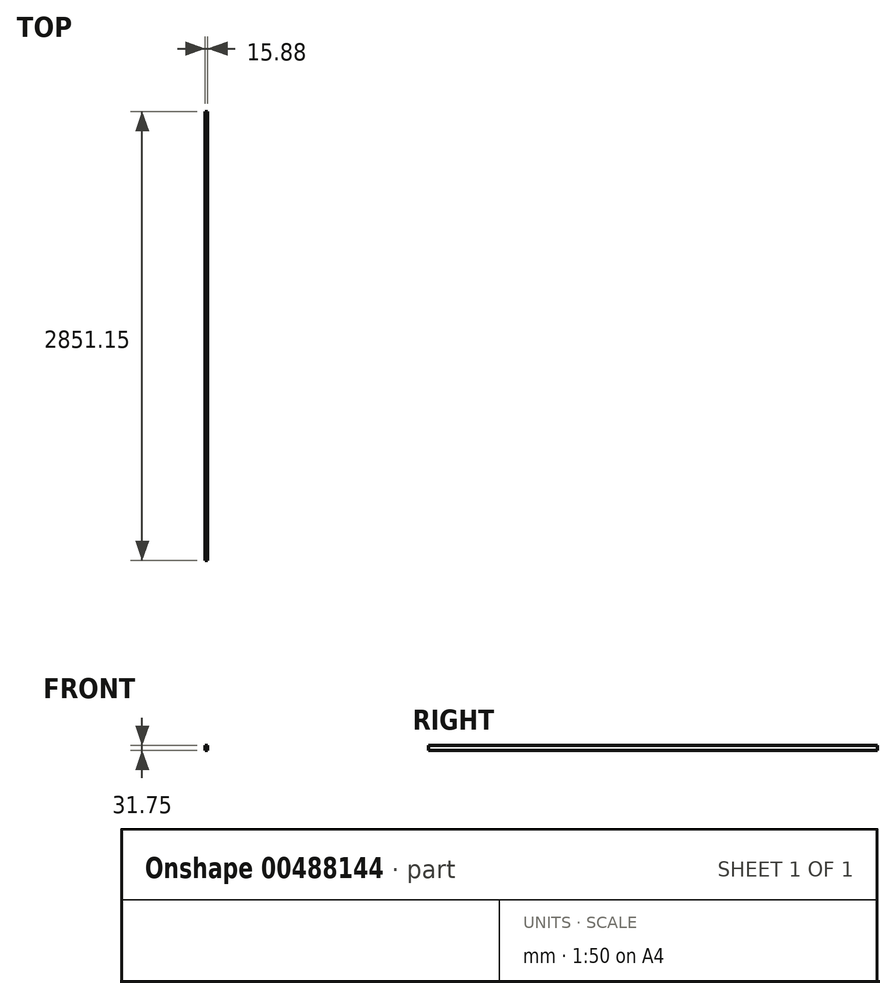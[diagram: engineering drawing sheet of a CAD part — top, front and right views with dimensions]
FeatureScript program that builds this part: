
annotation { "Feature Type Name" : "Feature", "Feature Type Description" : "" }
export const myFeature = defineFeature(function(context is Context, id is Id, definition is map)
    precondition{}
    {
        {
            var Q0;
            Q0=qCreatedBy(makeId("Front.planeOp"),FACE);
            var sketch = newSketch(context, id + "F0", { "sketchPlane" : qUnion([Q0])});
            skLineSegment(sketch, "E0", {"start": v(0, 0) * mm, "end": v(15.88, 0) * mm});
            skLineSegment(sketch, "E1", {"start": v(0, 0) * mm, "end": v(0, -31.75) * mm});
            skLineSegment(sketch, "E2", {"start": v(0, -31.75) * mm, "end": v(15.88, -31.75) * mm});
            skLineSegment(sketch, "E3", {"start": v(15.88, -31.75) * mm, "end": v(15.88, 0) * mm});
            skSolve(sketch);
        }
        {
            var Q0;
            Q0=makeQuery(id+"F0.imprint","IMPRINT",FACE,{"disambiguationData":[TD([[makeQuery(id+"F0.imprint","IMPRINT",EDGE,{"derivedFrom":sQuery(id+"F0.wireOp",EDGE,"E0")}),-1.0]])]});
            var Q1;
            Q1=makeQuery(id+"F0.imprint","IMPRINT",FACE,{"disambiguationData":[TD([[makeQuery(id+"F0.imprint","IMPRINT",EDGE,{"derivedFrom":sQuery(id+"F0.wireOp",EDGE,"E0")}),-1.0]])]});
            var Q2;
            Q2=makeQuery(id+"F0.imprint","IMPRINT",FACE,{"disambiguationData":[TD([[makeQuery(id+"F0.imprint","IMPRINT",EDGE,{"derivedFrom":sQuery(id+"F0.wireOp",EDGE,"sE00Gzr5-o4TN-UCdV-R85f-zcs0Y7AX2MqQ")}),1.0]])]});
            extrude(context, id + "F1", {"entities" : qUnion([Q0, Q1, Q2]), "depth" : 2851.15 * mm, "offsetDistance" : 25.4 * mm});
        }
    });
